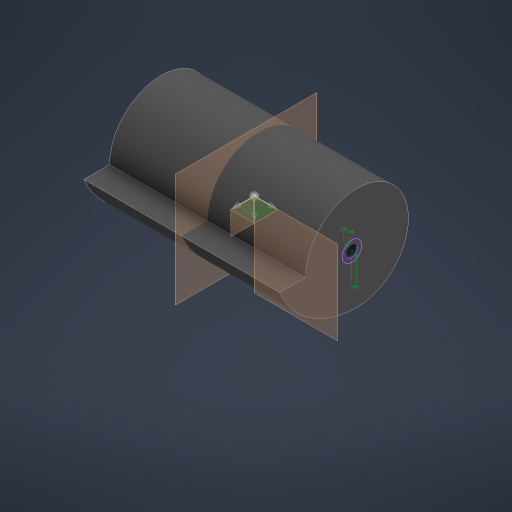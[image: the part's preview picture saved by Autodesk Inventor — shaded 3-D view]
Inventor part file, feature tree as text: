
AUTODESK INVENTOR PART (.ipt)
format: ipt  version: 2024.1 (Build 281209000, 209)  size: 200,192 bytes
history: native  units: in
note: dims shown in document units (in); Inventor stores cm internally (conversion verified against a paired STEP export)
features: extrude x3, sketch x2, plane x1
ambient origin geometry x8: Origin, YZ Plane, XZ Plane, XY Plane, X Axis, Y Axis, Z Axis, Center Point
bodies: Solid1 (feature_tree)
feature tree (6):
  extrude  "Extrusion1"  Depth=0.5in
  plane  "Work Plane1"
  sketch  "Sketch2"  dims[d2=3.8in d3=0.0in d4=0.1in d5=0.23in d6=0.375in d7=0.5in d8=0.0in d9=0.55in d10=0.0in d11=0.18in]
  extrude  "Extrusion2"  Depth=0.55in
  extrude  "Extrusion3"  Depth=0.55in
  sketch  "Sketch1"  dims[d0=2.0in d1=0.5in]
